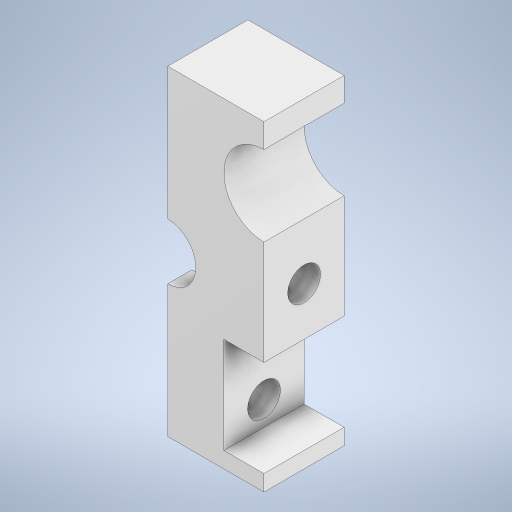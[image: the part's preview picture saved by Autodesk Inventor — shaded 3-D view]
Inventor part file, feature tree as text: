
AUTODESK INVENTOR PART (.ipt)
format: ipt  version: 2023 (Build 270158000, 158)  size: 325,120 bytes
history: native  units: mm
features: extrude x7, sketch x7, plane x1
ambient origin geometry x8: Origin, YZ Plane, XZ Plane, XY Plane, X Axis, Y Axis, Z Axis, Center Point
bodies: Solid1 (feature_tree)
feature tree (15):
  extrude  "Extrusion1"  Depth=20.0mm
  plane  "Work Plane1"
  extrude  "Extrusion2"  Depth=2.0mm
  extrude  "Extrusion3"  Depth=4.0mm
  extrude  "Extrusion4"  Depth=5.0mm TaperAngle=0.0deg
  extrude  "Extrusion5"  Depth=5.0mm TaperAngle=0.0deg
  extrude  "Extrusion6"  Depth=8.0mm TaperAngle=0.0deg
  extrude  "Extrusion7"  Depth=10.0mm
  sketch  "Sketch1"  dims[d0=20.0mm d1=20.0mm]
  sketch  "Sketch2"  dims[d2=4.0mm d6=2.0mm]
  sketch  "Sketch3"  dims[d7=2.0mm d8=4.0mm]
  sketch  "Sketch4"  dims[d9=2.0mm d10=5.0mm d11=0.0mm]
  sketch  "Sketch5"  dims[d12=5.0mm d13=2.0mm d14=0.0mm]
  sketch  "Sketch6"  dims[d15=3.5mm d16=8.0mm d17=0.0mm]
  sketch  "Sketch7"  dims[d18=2.05mm d19=2.05mm d20=2.5mm d21=2.5mm d22=2.5mm d23=2.5mm d24=25.0mm d25=0.0mm d30=5.0mm d31=0.0mm d32=2.5mm d33=1.0mm d34=6.0mm d35=5.0mm d36=4.0mm d37=5.0mm d38=0.0mm d39=2.5mm d40=10.0mm d41=2.05mm d42=12.0mm d43=0.0mm d44=6.0mm]
